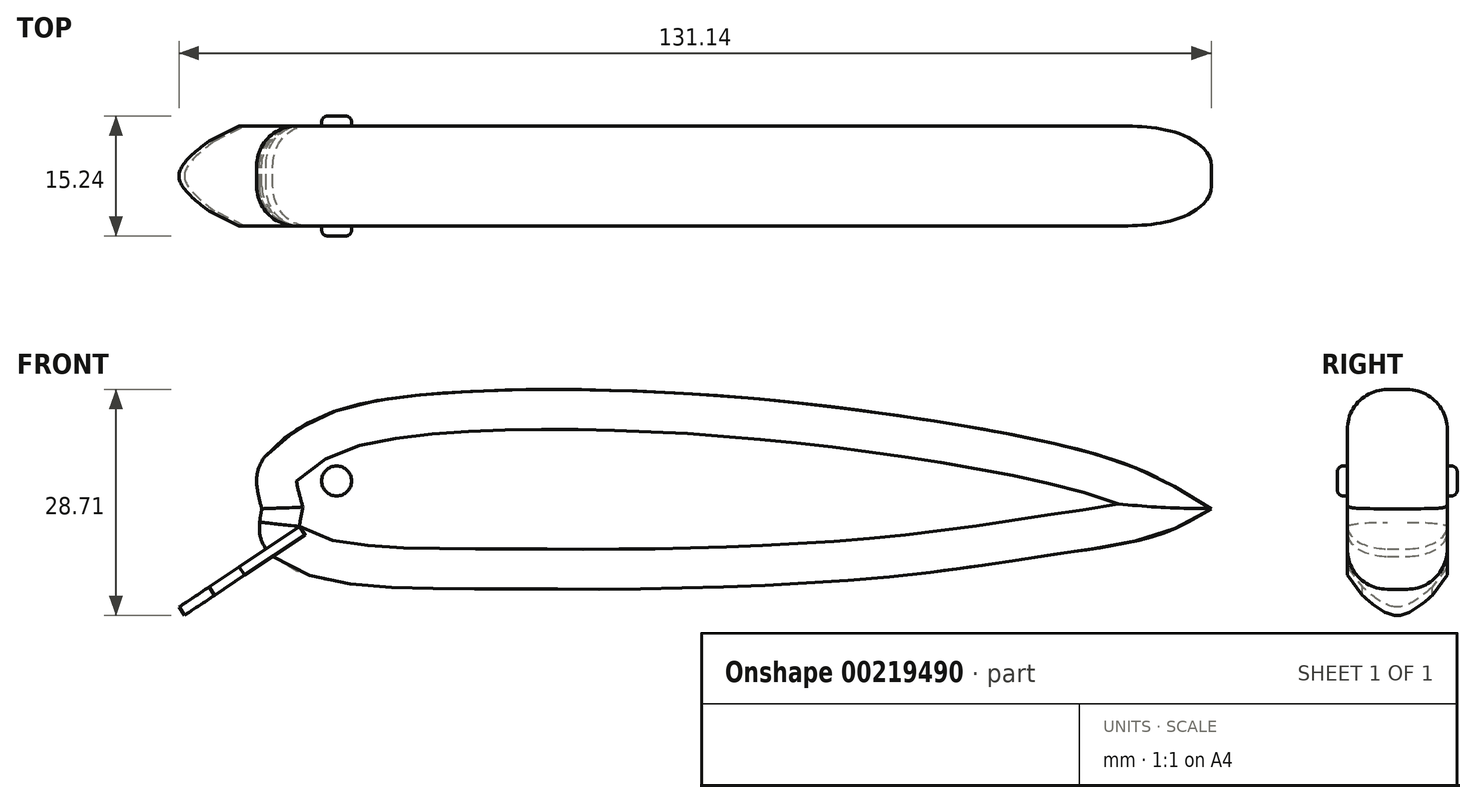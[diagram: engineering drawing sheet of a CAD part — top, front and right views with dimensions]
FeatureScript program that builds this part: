
annotation { "Feature Type Name" : "Feature", "Feature Type Description" : "" }
export const myFeature = defineFeature(function(context is Context, id is Id, definition is map)
    precondition{}
    {
        {
            var Q0;
            Q0=qCreatedBy(makeId("Front.planeOp"),FACE);
            var sketch = newSketch(context, id + "F0", { "sketchPlane" : qUnion([Q0])});
            skFitSpline(sketch, "E0", {"points": [v(-49.17, -0.25) * mm, v(-49.57, 4.95) * mm, v(-44.76, 9.76) * mm, v(-35.15, 13.37) * mm, v(1.27, 14.57) * mm, v(40.59, 10.16) * mm, v(61.82, 4.95) * mm, v(71.44, -0.25) * mm], "startDerivative": vector(-18.25, 66.84) * mm, "endDerivative": vector(74.48, -47.31) * mm});
            skFitSpline(sketch, "E1", {"points": [v(-49.17, -0.25) * mm, v(-49.17, -4.4) * mm, v(-42.84, -8.82) * mm, v(-21.2, -10.42) * mm, v(0, -10.42) * mm, v(31.32, -8.82) * mm, v(51.76, -6.01) * mm, v(64.59, -3.6) * mm, v(71.44, -0.25) * mm], "startDerivative": vector(-12.23, -63.83) * mm, "endDerivative": vector(69.29, 41.06) * mm});
            skSolve(sketch);
        }
        {
            var Q0;
            Q0=makeQuery(id+"F0.imprint","IMPRINT",FACE,{"disambiguationData":[TD([[makeQuery(id+"F0.imprint","IMPRINT",EDGE,{"derivedFrom":sQuery(id+"F0.wireOp",EDGE,"E0")}),-1.0]])]});
            extrude(context, id + "F1", {"entities" : qUnion([Q0]), "depth" : 12.7 * mm});
        }
        {
            var Q0;
            Q0=makeQuery(id+"F1.opExtrude","CAP_FACE",FACE,{"disambiguationData":[OSD([sQuery(id+"F0.wireOp",EDGE,"E0"),sQuery(id+"F0.wireOp",EDGE,"E1")])],"isStart":false});
            var Q1;
            Q1=makeQuery(id+"F1.opExtrude","CAP_FACE",FACE,{"disambiguationData":[OSD([sQuery(id+"F0.wireOp",EDGE,"E0"),sQuery(id+"F0.wireOp",EDGE,"E1")])],"isStart":true});
            fillet(context, id + "F2", {"entities" : qUnion([Q0, Q1]), "radius" : 5.08 * mm, "tangentPropagation" : true, "allowEdgeOverflow" : false});
        }
        {
            var Q0;
            Q0=makeQuery(id+"F1.opExtrude","CAP_FACE",FACE,{"disambiguationData":[OSD([sQuery(id+"F0.wireOp",EDGE,"E0"),sQuery(id+"F0.wireOp",EDGE,"E1")])],"isStart":false});
            var sketch = newSketch(context, id + "F3", { "sketchPlane" : qUnion([Q0])});
            skLineSegment(sketch, "E2", {"start": v(-44.4, -2.5) * mm, "end": v(-59.7, -12.75) * mm});
            skLineSegment(sketch, "E3.0", {"start": v(-43.69, -3.55) * mm, "end": v(-59, -13.8) * mm});
            skLineSegment(sketch, "E4", {"start": v(-59, -13.8) * mm, "end": v(-59.7, -12.75) * mm});
            skLineSegment(sketch, "E5", {"start": v(-43.69, -3.55) * mm, "end": v(-44.4, -2.5) * mm});
            skSolve(sketch);
        }
        {
            var Q0;
            Q0=makeQuery(id+"F3.imprint","IMPRINT",FACE,{"disambiguationData":[TD([[makeQuery(id+"F3.imprint","IMPRINT",EDGE,{"derivedFrom":sQuery(id+"F3.wireOp",EDGE,"E2")}),1.0]])]});
            extrude(context, id + "F4", {"entities" : qUnion([Q0]), "operationType" : NewBodyOperationType.ADD, "oppositeDirection" : true, "depth" : 12.7 * mm});
        }
        {
            var Q0;
            Q0=makeQuery(id+"F1.opExtrude","CAP_FACE",FACE,{"disambiguationData":[OSD([sQuery(id+"F0.wireOp",EDGE,"E0"),sQuery(id+"F0.wireOp",EDGE,"E1")])],"isStart":false});
            var sketch = newSketch(context, id + "F5", { "sketchPlane" : qUnion([Q0])});
            skLineSegment(sketch, "E6", {"start": v(-44.75, 3.28) * mm, "end": v(-39.67, 3.28) * mm, "construction": true});
            skCircle(sketch, "E7", {"center": v(-39.67, 3.28) * mm, "radius": 1.9 * mm});
            skSolve(sketch);
        }
        {
            var Q0;
            Q0=makeQuery(id+"F1.opExtrude","CAP_FACE",FACE,{"disambiguationData":[OSD([sQuery(id+"F0.wireOp",EDGE,"E0"),sQuery(id+"F0.wireOp",EDGE,"E1")])],"isStart":true});
            var sketch = newSketch(context, id + "F6", { "sketchPlane" : qUnion([Q0])});
            skLineSegment(sketch, "E8", {"start": v(44.75, 3.28) * mm, "end": v(39.67, 3.28) * mm, "construction": true});
            skCircle(sketch, "E9", {"center": v(39.67, 3.28) * mm, "radius": 1.9 * mm});
            skSolve(sketch);
        }
        {
            var Q0;
            Q0=makeQuery(id+"F6.imprint","IMPRINT",FACE,{"disambiguationData":[TD([[makeQuery(id+"F6.imprint","IMPRINT",EDGE,{"derivedFrom":sQuery(id+"F6.wireOp",EDGE,"E9")}),1.0]])]});
            var Q1;
            Q1=sQuery(id+"F6.wireOp",EDGE,"E9");
            extrude(context, id + "F7", {"entities" : qUnion([Q0]), "operationType" : NewBodyOperationType.ADD, "surfaceEntities" : qUnion([Q1]), "depth" : 1.27 * mm});
        }
        {
            var Q0;
            Q0=makeQuery(id+"F5.imprint","IMPRINT",FACE,{"disambiguationData":[TD([[makeQuery(id+"F5.imprint","IMPRINT",EDGE,{"derivedFrom":sQuery(id+"F5.wireOp",EDGE,"E7")}),1.0]])]});
            var Q1;
            Q1=sQuery(id+"F5.wireOp",EDGE,"E7");
            extrude(context, id + "F8", {"entities" : qUnion([Q0]), "operationType" : NewBodyOperationType.ADD, "surfaceEntities" : qUnion([Q1]), "depth" : 1.27 * mm});
        }
        {
            var Q0;
            Q0=makeQuery(id+"F8.opExtrude","CAP_FACE",FACE,{"disambiguationData":[OSD([sQuery(id+"F5.wireOp",EDGE,"E7")])],"isStart":false});
            fillet(context, id + "F9", {"entities" : qUnion([Q0]), "radius" : 0.76 * mm, "tangentPropagation" : true, "allowEdgeOverflow" : false});
        }
        {
            var Q0;
            Q0=makeQuery(id+"F7.opExtrude","CAP_FACE",FACE,{"disambiguationData":[OSD([sQuery(id+"F6.wireOp",EDGE,"E9")])],"isStart":false});
            fillet(context, id + "F10", {"entities" : qUnion([Q0]), "radius" : 0.76 * mm, "tangentPropagation" : true, "allowEdgeOverflow" : false});
        }
        {
            var Q0;
            Q0=makeQuery(id+"F4.opExtrude","SWEPT_FACE",FACE,{"disambiguationData":[OSD([sQuery(id+"F3.wireOp",EDGE,"E2")])]});
            var sketch = newSketch(context, id + "F11", { "sketchPlane" : qUnion([Q0])});
            skLineSegment(sketch, "E10", {"start": v(-47.48, -12.7) * mm, "end": v(-56.69, -8.9) * mm});
            skLineSegment(sketch, "E11", {"start": v(-47.48, 0) * mm, "end": v(-56.69, -3.81) * mm});
            skLineSegment(sketch, "E12", {"start": v(-47.48, 0) * mm, "end": v(-56.69, 0) * mm});
            skLineSegment(sketch, "E13", {"start": v(-56.69, 0) * mm, "end": v(-56.69, -3.81) * mm});
            skLineSegment(sketch, "E14", {"start": v(-56.69, -8.9) * mm, "end": v(-56.69, -12.7) * mm});
            skLineSegment(sketch, "E15", {"start": v(-56.69, -12.7) * mm, "end": v(-47.48, -12.7) * mm});
            skFitSpline(sketch, "E16", {"points": [v(-52.08, -1.9) * mm, v(-56.69, -6.35) * mm, v(-52.08, -10.8) * mm], "startDerivative": vector(-13.82, -8.9) * mm, "endDerivative": vector(13.82, -8.89) * mm});
            skLineSegment(sketch, "E17", {"start": v(-56.69, -3.81) * mm, "end": v(-56.69, -6.35) * mm});
            skLineSegment(sketch, "E18", {"start": v(-56.69, -8.9) * mm, "end": v(-56.69, -6.35) * mm});
            skSolve(sketch);
        }
        {
            var Q0;
            {var subQ0=sQuery(id+"F11.wireOp",EDGE,"E12");Q0=makeQuery(id+"F11.imprint","IMPRINT",FACE,{"disambiguationData":[TD([[makeQuery(id+"F11.imprint","IMPRINT",EDGE,{"derivedFrom":subQ0}),1.0]])]});}
            extrude(context, id + "F12", {"entities" : qUnion([Q0]), "operationType" : NewBodyOperationType.REMOVE, "endBound" : BoundingType.UP_TO_NEXT, "oppositeDirection" : true, "depth" : 25.4 * mm});
        }
        {
            var Q0;
            {var subQ0=sQuery(id+"F11.wireOp",EDGE,"E17");Q0=makeQuery(id+"F11.imprint","IMPRINT",FACE,{"disambiguationData":[TD([[makeQuery(id+"F11.imprint","IMPRINT",EDGE,{"derivedFrom":subQ0}),1.0]])]});}
            var Q1;
            {var subQ0=sQuery(id+"F11.wireOp",EDGE,"E18");Q1=makeQuery(id+"F11.imprint","IMPRINT",FACE,{"disambiguationData":[TD([[makeQuery(id+"F11.imprint","IMPRINT",EDGE,{"derivedFrom":subQ0}),1.0]])]});}
            var Q2;
            {var subQ3=sQuery(id+"F11.wireOp",EDGE,"E14");Q2=makeQuery(id+"F11.imprint","IMPRINT",FACE,{"disambiguationData":[TD([[makeQuery(id+"F11.imprint","IMPRINT",EDGE,{"derivedFrom":subQ3}),1.0]])]});}
            var Q3;
            {var subQ0=sQuery(id+"F11.wireOp",EDGE,"E12");Q3=makeQuery(id+"F11.imprint","IMPRINT",FACE,{"disambiguationData":[TD([[makeQuery(id+"F11.imprint","IMPRINT",EDGE,{"derivedFrom":subQ0}),1.0]])]});}
            extrude(context, id + "F13", {"entities" : qUnion([Q0, Q1, Q2, Q3]), "operationType" : NewBodyOperationType.REMOVE, "oppositeDirection" : true, "depth" : 5.08 * mm});
        }
    });
